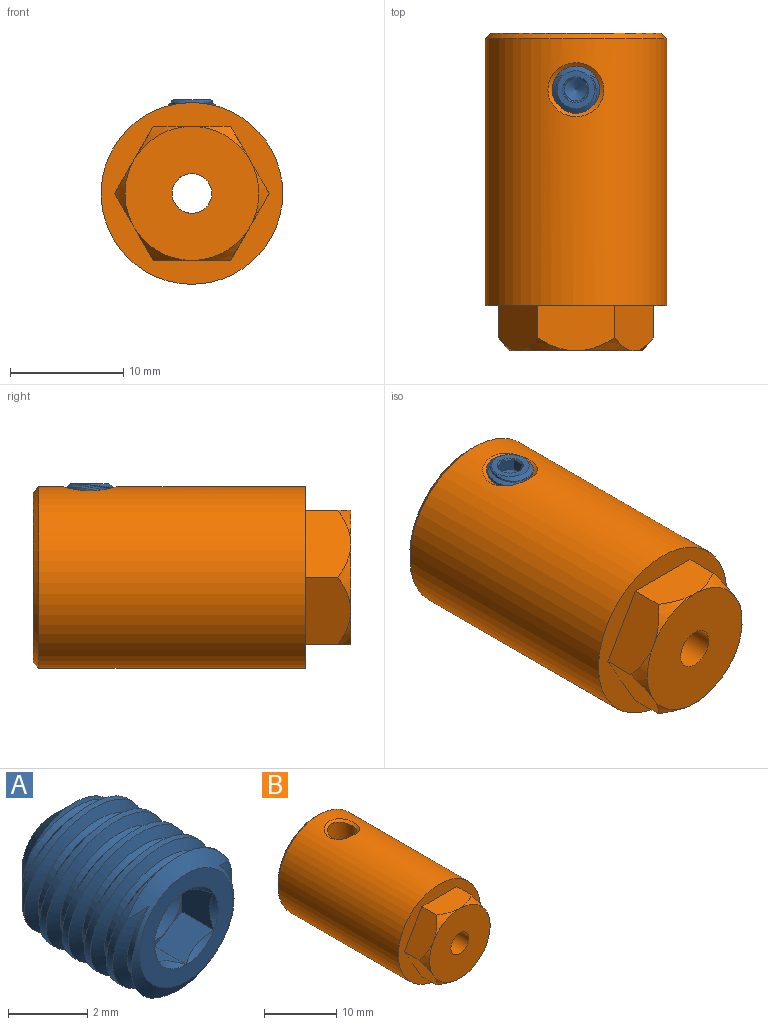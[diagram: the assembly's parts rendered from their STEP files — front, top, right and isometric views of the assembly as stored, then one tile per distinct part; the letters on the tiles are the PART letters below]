
ASSEMBLY  parts=2 mates=1
PART A: 47 faces, bbox 4.8x5.3x4.9 mm
  f0: cone r=0.99mm half-angle=59deg, axis (0,-1,0), area 3.6mm2, adj f1,f42,f43,f44,f45,f46
  f1: plane 0.86x0.5mm, normal (0,-1,0), area 0.1mm2, adj f0,f2,f41
  f2: plane 1.26x1.25mm, normal (-1,0,0), area 1.2mm2, adj f1,f3,f40,f41,f42
  f3: plane 1.58x1.43mm, normal (-0.5,0,-0.87), area 1.2mm2, adj f2,f4,f39,f42,f43
  f4: plane 1.58x1.43mm, normal (0.5,0,-0.87), area 1.2mm2, adj f3,f5,f38,f43,f44
  f5: plane 1.58x1.58mm, normal (1,0,0), area 1.2mm2, adj f4,f6,f37,f44,f45
  f6: plane 1.58x1.43mm, normal (0.5,0,0.87), area 1.2mm2, adj f5,f7,f41,f45,f46
  f7: cone r=1.15mm half-angle=45deg, axis (0,-1,0), area 0mm2, adj f6,f8
  f8: plane 3.33x3.33mm, normal (0,-1,0), area 4.6mm2, adj f7,f9,f10,f37,f38,f39,f40
  f9: cone r=1.15mm half-angle=45deg, axis (0,-1,0), area 0mm2, adj f8,f41
  f10: cone r=2.08mm half-angle=55deg, axis (0,1,0), area 4.3mm2, adj f8,f11,f12,f13,f14,f15,f16
  f11: cylinder r=2.08mm len=1.94mm, axis (0,-1,0), area 0mm2, adj f10,f12
  f12: cone r=2.21mm half-angle=60deg, axis (0,-0.98,-0.19), area 1.4mm2, adj f10,f11,f13
  f13: cylinder r=1.78mm len=3.55mm, axis (0,0.98,0.19), area 1.4mm2, adj f10,f12,f14
  f14: cone r=1.78mm half-angle=60deg, axis (0,0.98,0.19), area 3.4mm2, adj f10,f13,f15
  f15: cylinder r=2.08mm len=4.17mm, axis (0,-1,0), area 2.1mm2, adj f10,f14,f16
  f16: cone r=2.21mm half-angle=60deg, axis (0,-0.98,-0.19), area 5mm2, adj f10,f15,f17
  f17: cylinder r=1.78mm len=3.55mm, axis (0,0.98,0.19), area 2.2mm2, adj f16,f18
  f18: cone r=1.78mm half-angle=60deg, axis (0,0.98,0.19), area 4.8mm2, adj f17,f19
  f19: cylinder r=2.08mm len=4.17mm, axis (0,-1,0), area 2.7mm2, adj f18,f20
  f20: cone r=2.21mm half-angle=60deg, axis (0,-0.98,-0.19), area 5mm2, adj f19,f21
  f21: cylinder r=1.78mm len=3.55mm, axis (0,0.98,0.19), area 2.2mm2, adj f20,f22
  f22: cone r=1.78mm half-angle=60deg, axis (0,0.98,0.19), area 4.8mm2, adj f21,f23
  f23: cylinder r=2.08mm len=4.17mm, axis (0,-1,0), area 2.7mm2, adj f22,f24
  f24: cone r=2.21mm half-angle=60deg, axis (0,-0.98,-0.19), area 5mm2, adj f23,f25
  f25: cylinder r=1.78mm len=3.55mm, axis (0,0.98,0.19), area 2.2mm2, adj f24,f26
  f26: cone r=1.78mm half-angle=60deg, axis (0,0.98,0.19), area 4.8mm2, adj f25,f27
  f27: cylinder r=2.08mm len=4.17mm, axis (0,-1,0), area 2.7mm2, adj f26,f28
  f28: cone r=2.21mm half-angle=60deg, axis (0,-0.98,-0.19), area 5mm2, adj f27,f29
  f29: cylinder r=1.78mm len=3.55mm, axis (0,0.98,0.19), area 2.2mm2, adj f28,f30
  f30: cone r=1.78mm half-angle=60deg, axis (0,0.98,0.19), area 4mm2, adj f29,f31,f36
  f31: cone r=1.1mm half-angle=45deg, axis (0,-1,0), area 11mm2, adj f30,f32,f33,f34,f35,f36
  f32: cone r=1.78mm half-angle=60deg, axis (0,0.98,0.19), area 0.2mm2, adj f31,f33
  f33: cylinder r=1.78mm len=3.55mm, axis (0,0.98,0.19), area 0.9mm2, adj f31,f32,f34
  f34: cone r=2.21mm half-angle=60deg, axis (0,-0.98,-0.19), area 2.1mm2, adj f31,f33,f36
  f35: cone r=1664.28mm half-angle=59deg, axis (0,1,0), area 4.5mm2, adj f31
  f36: cylinder r=2.08mm len=4.17mm, axis (0,-1,0), area 2mm2, adj f30,f31,f34
  f37: cone r=1.15mm half-angle=45deg, axis (0,-1,0), area 0mm2, adj f5,f8
  f38: cone r=1.15mm half-angle=45deg, axis (0,-1,0), area 0mm2, adj f4,f8
  f39: cone r=1.15mm half-angle=45deg, axis (0,-1,0), area 0mm2, adj f3,f8
  f40: cone r=1.15mm half-angle=45deg, axis (0,-1,0), area 0.1mm2, adj f2,f8
  f41: plane 1.58x1.43mm, normal (-0.5,0,0.87), area 1.2mm2, adj f1,f2,f6,f9,f46
  f42: plane 0.86x0.5mm, normal (0,-1,0), area 0.1mm2, adj f0,f2,f3
  f43: plane 0.99x0.29mm, normal (0,-1,0), area 0.1mm2, adj f0,f3,f4
  f44: plane 0.86x0.5mm, normal (0,-1,0), area 0.1mm2, adj f0,f4,f5
  f45: plane 0.86x0.5mm, normal (0,-1,0), area 0.1mm2, adj f0,f5,f6
  f46: plane 0.99x0.29mm, normal (0,-1,0), area 0.1mm2, adj f0,f6,f41
PART B: 23 faces, bbox 16.7x28.7x16.7 mm
  f0: bspline ~4.93x4.75mm, area 7.1mm2, adj f4,f7
  f1: cone r=5.9mm half-angle=38.7deg, axis (0,1,0), area 4.7mm2, adj f14,f15,f16
  f2: cone r=3.02mm half-angle=45deg, axis (0,1,0), area 14.6mm2, adj f6,f9
  f3: cone r=8mm half-angle=45deg, axis (0,-1,0), area 34.4mm2, adj f7,f9
  f4: cylinder r=2mm len=4.69mm, axis (0,0,-1), area 58.9mm2, adj f0,f6
  f5: cylinder r=1.75mm len=8mm, axis (0,-1,0), area 88mm2, adj f16,f17
  f6: cylinder r=3.02mm len=19.5mm, axis (0,1,0), area 357.2mm2, adj f2,f4,f17
  f7: cylinder r=8mm len=23.5mm, axis (0,1,0), area 1162.6mm2, adj f0,f3,f8
  f8: plane 16x16mm, normal (0,-1,0), area 80.5mm2, adj f7,f10,f11,f12,f13,f14,f15
  f9: plane 15x15mm, normal (0,1,0), area 137.7mm2, adj f2,f3
  f10: plane 7.55x4.73mm, normal (0,0,-1), area 24.6mm2, adj f8,f11,f15,f21,f22
  f11: plane 6.63x4.73mm, normal (0.87,0,-0.5), area 24.6mm2, adj f8,f10,f12,f18,f22
  f12: plane 6.63x4.73mm, normal (0.87,0,0.5), area 24.6mm2, adj f8,f11,f13,f18,f19
  f13: plane 7.55x4.73mm, normal (0,0,1), area 24.6mm2, adj f8,f12,f14,f19,f20
  f14: plane 6.63x4.73mm, normal (-0.87,0,0.5), area 24.6mm2, adj f1,f8,f13,f15,f20
  f15: plane 6.63x4.73mm, normal (-0.87,0,-0.5), area 24.6mm2, adj f1,f8,f10,f14,f21
  f16: plane 11.8x11.8mm, normal (0,-1,0), area 99.7mm2, adj f1,f5,f18,f19,f20,f21,f22
  f17: plane 6.05x6.05mm, normal (0,1,0), area 19.1mm2, adj f5,f6
  f18: cone r=5.9mm half-angle=38.7deg, axis (0,1,0), area 4.7mm2, adj f11,f12,f16
  f19: cone r=5.9mm half-angle=38.7deg, axis (0,1,0), area 4.7mm2, adj f12,f13,f16
  f20: cone r=5.9mm half-angle=38.7deg, axis (0,1,0), area 4.7mm2, adj f13,f14,f16
  f21: cone r=5.9mm half-angle=38.7deg, axis (0,1,0), area 4.7mm2, adj f10,f15,f16
  f22: cone r=5.9mm half-angle=38.7deg, axis (0,1,0), area 4.7mm2, adj f10,f11,f16
PLACE A rot(axis=(-1,0,0),90deg) t=(0,0,2.71)mm
PLACE B t=(-7.12,13.33,-19.4)mm
MATE fastened A.f35 <-> B.f4  axis (0,0,1) through (0,0,4.76)mm
